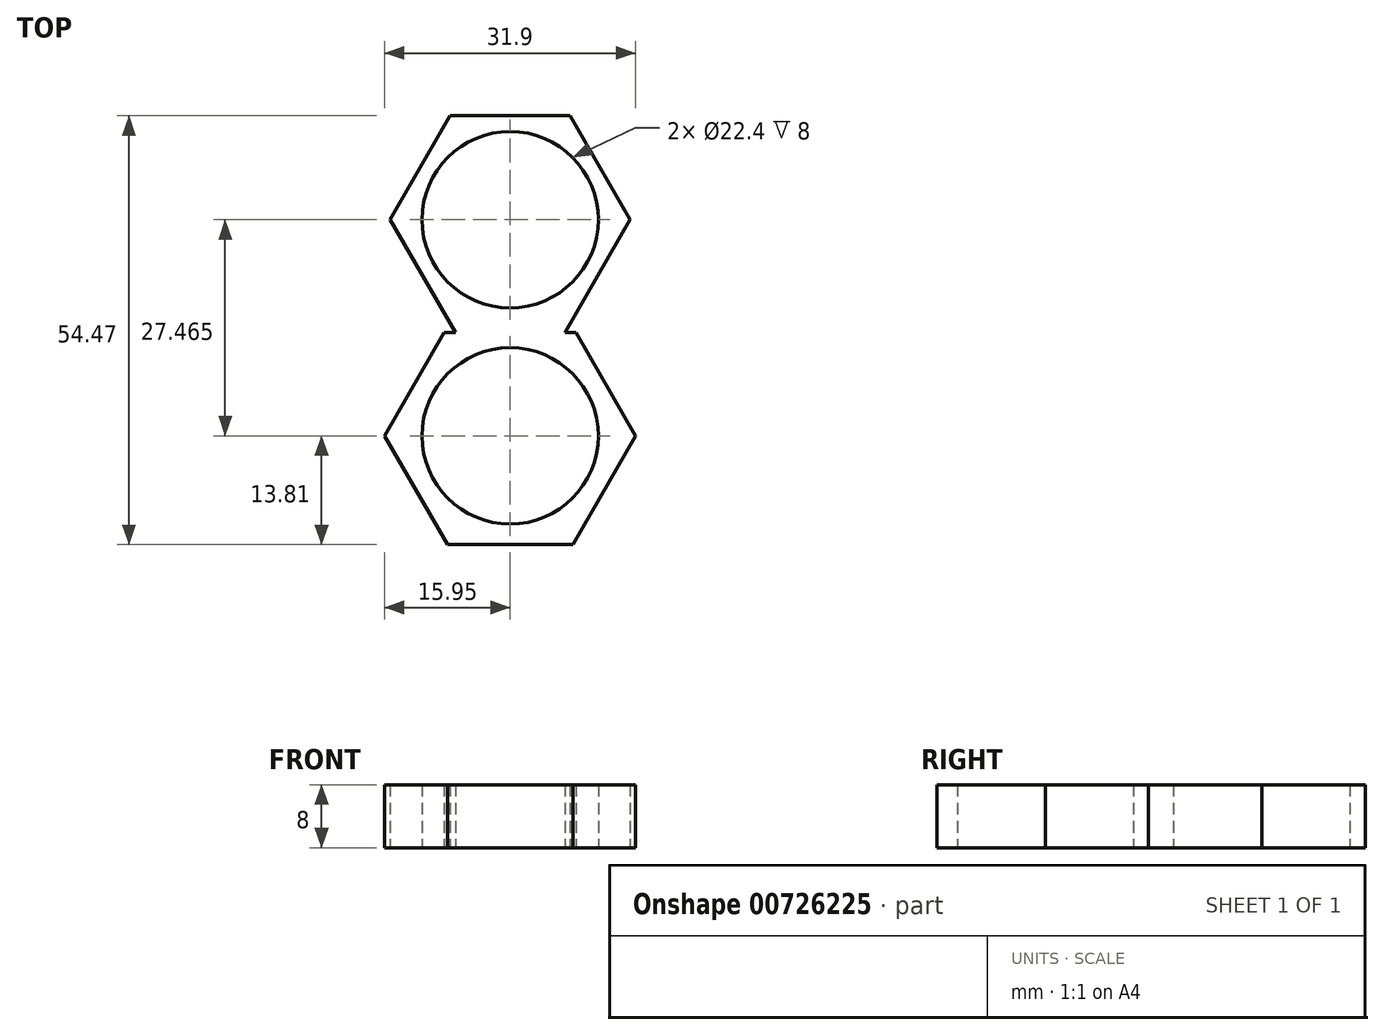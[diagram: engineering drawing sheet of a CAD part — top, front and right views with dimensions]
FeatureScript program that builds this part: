
annotation { "Feature Type Name" : "Feature", "Feature Type Description" : "" }
export const myFeature = defineFeature(function(context is Context, id is Id, definition is map)
    precondition{}
    {
        {
            var Q0;
            Q0=qCreatedBy(makeId("Top.planeOp"),FACE);
            var sketch = newSketch(context, id + "F0", { "sketchPlane" : qUnion([Q0])});
            skLineSegment(sketch, "E0.0", {"start": v(-8.38, 13.1) * mm, "end": v(8.38, 13.1) * mm});
            skLineSegment(sketch, "E0.1", {"start": v(8.38, 13.1) * mm, "end": v(15.95, 0) * mm});
            skLineSegment(sketch, "E0.2", {"start": v(15.95, 0) * mm, "end": v(7.98, -13.81) * mm});
            skLineSegment(sketch, "E0.3", {"start": v(7.98, -13.81) * mm, "end": v(-7.98, -13.81) * mm});
            skLineSegment(sketch, "E0.4", {"start": v(-7.98, -13.81) * mm, "end": v(-15.95, 0) * mm});
            skLineSegment(sketch, "E0.5", {"start": v(-15.95, 0) * mm, "end": v(-8.38, 13.1) * mm});
            skPoint(sketch, "E0.0.midPoint", {"position": v(0, 13.1) * mm});
            skPoint(sketch, "E0.cCircle.center.orphan", {"position": v(0, 0) * mm});
            skCircle(sketch, "E1", {"center": v(0, 0) * mm, "radius": 11.2 * mm});
            skPoint(sketch, "E2.0.midPoint", {"position": v(0, 40.66) * mm});
            skPoint(sketch, "E3.orphan", {"position": v(7.62, 38.78) * mm});
            skPoint(sketch, "E2.5.end.orphan", {"position": v(-7.62, 42.55) * mm});
            skPoint(sketch, "E4.center.orphan", {"position": v(0, 27.46) * mm});
            skLineSegment(sketch, "E5.0", {"start": v(-7.62, 40.66) * mm, "end": v(7.62, 40.66) * mm});
            skLineSegment(sketch, "E5.1", {"start": v(7.62, 40.66) * mm, "end": v(15.24, 27.46) * mm});
            skLineSegment(sketch, "E5.2", {"start": v(15.24, 27.46) * mm, "end": v(6.8, 12.85) * mm});
            skLineSegment(sketch, "E5.3", {"start": v(6.8, 12.85) * mm, "end": v(-6.8, 12.85) * mm});
            skLineSegment(sketch, "E5.4", {"start": v(-6.8, 12.85) * mm, "end": v(-15.24, 27.46) * mm});
            skLineSegment(sketch, "E5.5", {"start": v(-15.24, 27.46) * mm, "end": v(-7.62, 40.66) * mm});
            skCircle(sketch, "E6", {"center": v(0, 27.46) * mm, "radius": 11.2 * mm});
            skSolve(sketch);
        }
        {
            var Q0;
            Q0 = qSketchRegion(id + "F0", true);
            extrude(context, id + "F1", {"entities" : qUnion([Q0]), "depth" : 7 * mm, "offsetDistance" : 25 * mm});
        }
        {
            var Q0;
            Q0 = qSketchRegion(id + "F0", true);
            extrude(context, id + "F2", {"entities" : qUnion([Q0]), "operationType" : NewBodyOperationType.ADD, "depth" : 8 * mm, "offsetDistance" : 25 * mm});
        }
    });
